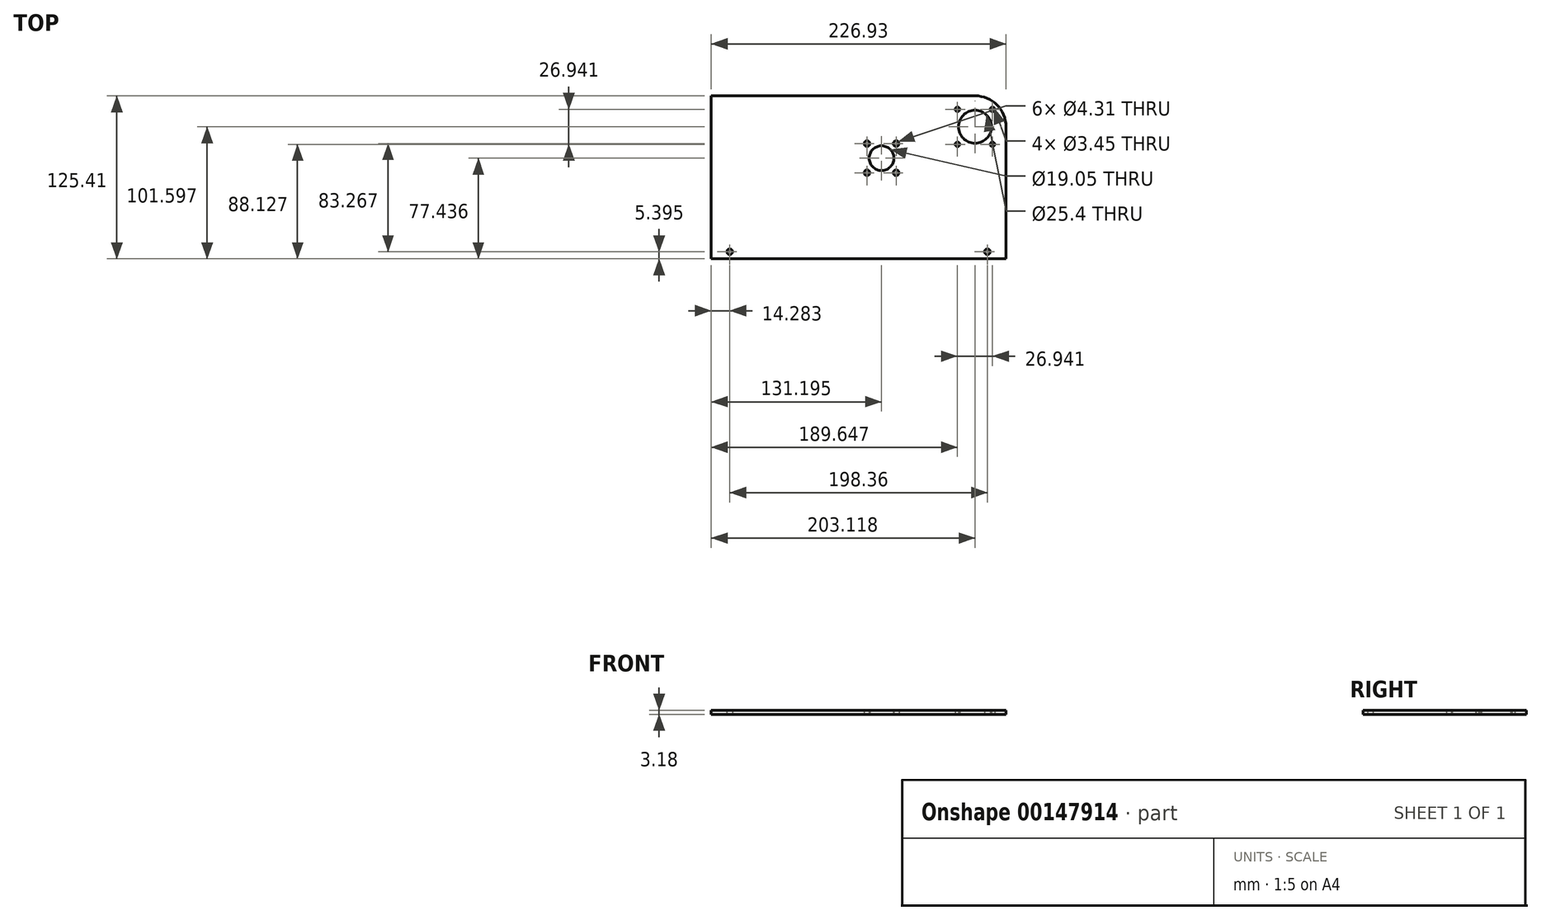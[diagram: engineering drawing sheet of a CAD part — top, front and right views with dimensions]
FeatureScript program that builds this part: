
annotation { "Feature Type Name" : "Feature", "Feature Type Description" : "" }
export const myFeature = defineFeature(function(context is Context, id is Id, definition is map)
    precondition{}
    {
        {
            var Q0;
            Q0=qCreatedBy(makeId("Top.planeOp"),FACE);
            var sketch = newSketch(context, id + "F0", { "sketchPlane" : qUnion([Q0])});
            skCircle(sketch, "E0", {"center": v(-23.81, -23.81) * mm, "radius": 14.29 * mm, "construction": true});
            skLineSegment(sketch, "E1.bottom", {"start": v(-226.93, 0) * mm, "end": v(0, 0) * mm});
            skLineSegment(sketch, "E1.top", {"start": v(-226.93, -125.41) * mm, "end": v(0, -125.41) * mm});
            skLineSegment(sketch, "E1.left", {"start": v(-226.93, 0) * mm, "end": v(-226.93, -125.41) * mm});
            skLineSegment(sketch, "E1.right", {"start": v(0, 0) * mm, "end": v(0, -125.41) * mm});
            skCircle(sketch, "E2", {"center": v(-23.81, -23.81) * mm, "radius": 23.81 * mm, "construction": true});
            skLineSegment(sketch, "E3", {"start": v(0, -120.02) * mm, "end": v(-14.29, -120.02) * mm, "construction": true});
            skLineSegment(sketch, "E4", {"start": v(-226.93, -120.02) * mm, "end": v(-212.65, -120.02) * mm, "construction": true});
            skLineSegment(sketch, "E5", {"start": v(-14.29, -120.02) * mm, "end": v(-14.29, -125.41) * mm, "construction": true});
            skCircle(sketch, "E6", {"center": v(-14.29, -120.02) * mm, "radius": 2.15 * mm});
            skCircle(sketch, "E7", {"center": v(-212.65, -120.02) * mm, "radius": 2.15 * mm});
            skLineSegment(sketch, "E8", {"start": v(-23.81, -23.81) * mm, "end": v(-95.74, -47.97) * mm, "construction": true});
            skCircle(sketch, "E9", {"center": v(-95.74, -47.97) * mm, "radius": 9.53 * mm});
            skLineSegment(sketch, "E10.bottom", {"start": v(-84.51, -59.2) * mm, "end": v(-106.96, -59.2) * mm, "construction": true});
            skLineSegment(sketch, "E10.top", {"start": v(-84.51, -36.75) * mm, "end": v(-106.96, -36.75) * mm, "construction": true});
            skLineSegment(sketch, "E10.left", {"start": v(-84.51, -59.2) * mm, "end": v(-84.51, -36.75) * mm, "construction": true});
            skLineSegment(sketch, "E10.right", {"start": v(-106.96, -59.2) * mm, "end": v(-106.96, -36.75) * mm, "construction": true});
            skCircle(sketch, "E11", {"center": v(-95.74, -47.97) * mm, "radius": 11.11 * mm, "construction": true});
            skCircle(sketch, "E12", {"center": v(-84.51, -36.75) * mm, "radius": 4.76 * mm, "construction": true});
            skCircle(sketch, "E13", {"center": v(-106.96, -36.75) * mm, "radius": 2.15 * mm});
            skCircle(sketch, "E14", {"center": v(-84.51, -36.75) * mm, "radius": 2.15 * mm});
            skCircle(sketch, "E15", {"center": v(-84.51, -59.2) * mm, "radius": 2.15 * mm});
            skCircle(sketch, "E16", {"center": v(-106.96, -59.2) * mm, "radius": 2.15 * mm});
            skCircle(sketch, "E17", {"center": v(-10.34, -10.34) * mm, "radius": 4.76 * mm, "construction": true});
            skLineSegment(sketch, "E18.bottom", {"start": v(-10.34, -37.28) * mm, "end": v(-37.28, -37.28) * mm, "construction": true});
            skLineSegment(sketch, "E18.top", {"start": v(-10.34, -10.34) * mm, "end": v(-37.28, -10.34) * mm, "construction": true});
            skLineSegment(sketch, "E18.left", {"start": v(-10.34, -37.28) * mm, "end": v(-10.34, -10.34) * mm, "construction": true});
            skLineSegment(sketch, "E18.right", {"start": v(-37.28, -37.28) * mm, "end": v(-37.28, -10.34) * mm, "construction": true});
            skCircle(sketch, "E19", {"center": v(-10.34, -10.34) * mm, "radius": 1.73 * mm});
            skCircle(sketch, "E20", {"center": v(-37.28, -10.34) * mm, "radius": 1.73 * mm});
            skCircle(sketch, "E21", {"center": v(-37.28, -37.28) * mm, "radius": 1.73 * mm});
            skCircle(sketch, "E22", {"center": v(-10.34, -37.28) * mm, "radius": 1.73 * mm});
            skCircle(sketch, "E23", {"center": v(-23.81, -23.81) * mm, "radius": 12.7 * mm});
            skSolve(sketch);
        }
        {
            var Q0;
            Q0=qSketchRegion(id+"F0",true);
            extrude(context, id + "F1", {"entities" : qUnion([Q0]), "depth" : 3.17 * mm});
        }
        {
            var Q0;
            Q0=makeQuery(id+"F1.opExtrude","SWEPT_EDGE",EDGE,{"disambiguationData":[OSD([sQuery(id+"F0.wireOp",EDGE,"E1.bottom"),sQuery(id+"F0.wireOp",EDGE,"E1.right")])]});
            fillet(context, id + "F2", {"entities" : qUnion([Q0]), "radius" : 23.8 * mm, "tangentPropagation" : true, "allowEdgeOverflow" : false});
        }
    });
